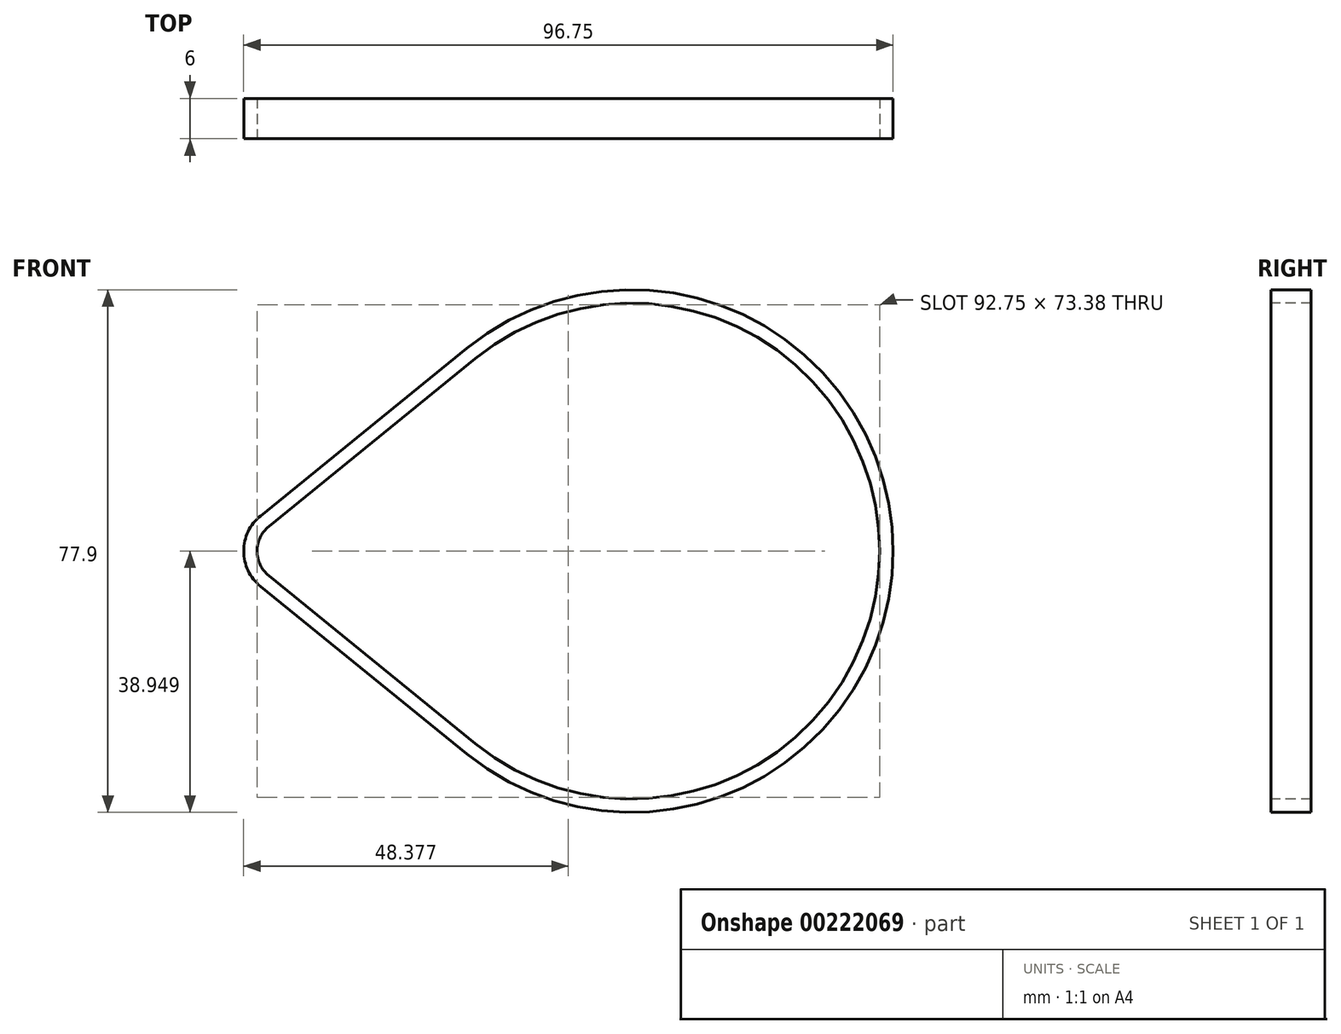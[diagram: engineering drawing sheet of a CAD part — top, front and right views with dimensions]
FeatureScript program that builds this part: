
annotation { "Feature Type Name" : "Feature", "Feature Type Description" : "" }
export const myFeature = defineFeature(function(context is Context, id is Id, definition is map)
    precondition{}
    {
        {
            var Q0;
            Q0=qCreatedBy(makeId("Front.planeOp"),FACE);
            var sketch = newSketch(context, id + "F0", { "sketchPlane" : qUnion([Q0])});
            skArc(sketch, "E0", {"start": v(89.5, 33.54) * mm, "mid": v(151.38, 62.99) * mm, "end": v(89.5, 92.44) * mm});
            skArc(sketch, "E1", {"start": v(58.76, 67.45) * mm, "mid": v(56.63, 62.99) * mm, "end": v(58.76, 58.53) * mm});
            skLineSegment(sketch, "E2", {"start": v(58.76, 67.45) * mm, "end": v(89.5, 92.44) * mm});
            skLineSegment(sketch, "E3", {"start": v(58.76, 58.53) * mm, "end": v(89.5, 33.54) * mm});
            skSolve(sketch);
        }
        {
            var Q0;
            Q0=makeQuery(id+"F0.imprint","IMPRINT",FACE,{"disambiguationData":[TD([[makeQuery(id+"F0.imprint","IMPRINT",EDGE,{"derivedFrom":sQuery(id+"F0.wireOp",EDGE,"E0")}),1.0]])]});
            extrude(context, id + "F1", {"entities" : qUnion([Q0]), "depth" : 6 * mm});
        }
        {
            var Q0;
            Q0=makeQuery(id+"F1.opExtrude","CAP_FACE",FACE,{"disambiguationData":[OSD([sQuery(id+"F0.wireOp",EDGE,"E0"),sQuery(id+"F0.wireOp",EDGE,"E1"),sQuery(id+"F0.wireOp",EDGE,"E2"),sQuery(id+"F0.wireOp",EDGE,"E3")])],"isStart":false});
            var sketch = newSketch(context, id + "F2", { "sketchPlane" : qUnion([Q0])});
            skLineSegment(sketch, "E4.0", {"start": v(58.76, 67.45) * mm, "end": v(89.5, 92.44) * mm});
            skArc(sketch, "E4.1", {"start": v(89.5, 33.54) * mm, "mid": v(151.38, 62.99) * mm, "end": v(89.5, 92.44) * mm});
            skLineSegment(sketch, "E5.0", {"start": v(58.76, 58.53) * mm, "end": v(89.5, 33.54) * mm});
            skArc(sketch, "E6.0", {"start": v(58.76, 67.45) * mm, "mid": v(56.63, 62.99) * mm, "end": v(58.76, 58.53) * mm});
            skLineSegment(sketch, "E7.0", {"start": v(59.39, 66.67) * mm, "end": v(90.13, 91.66) * mm});
            skArc(sketch, "E7.1", {"start": v(59.39, 66.67) * mm, "mid": v(57.63, 62.99) * mm, "end": v(59.39, 59.3) * mm});
            skLineSegment(sketch, "E7.2", {"start": v(59.39, 59.3) * mm, "end": v(90.13, 34.32) * mm});
            skArc(sketch, "E7.3", {"start": v(90.13, 34.32) * mm, "mid": v(150.38, 62.99) * mm, "end": v(90.13, 91.66) * mm});
            skSolve(sketch);
        }
        {
            var Q0;
            Q0=makeQuery(id+"F2.imprint","IMPRINT",FACE,{"disambiguationData":[TD([[makeQuery(id+"F2.imprint","IMPRINT",EDGE,{"derivedFrom":sQuery(id+"F2.wireOp",EDGE,"E7.0")}),-1.0]])]});
            extrude(context, id + "F3", {"entities" : qUnion([Q0]), "operationType" : NewBodyOperationType.REMOVE, "oppositeDirection" : true, "depth" : 25 * mm});
        }
        {
            var Q0;
            Q0=makeQuery(id+"F1.opExtrude","CAP_FACE",FACE,{"disambiguationData":[OSD([sQuery(id+"F0.wireOp",EDGE,"E0"),sQuery(id+"F0.wireOp",EDGE,"E1"),sQuery(id+"F0.wireOp",EDGE,"E2"),sQuery(id+"F0.wireOp",EDGE,"E3")])],"isStart":false});
            var sketch = newSketch(context, id + "F4", { "sketchPlane" : qUnion([Q0])});
            skLineSegment(sketch, "E8.0", {"start": v(58.12, 68.23) * mm, "end": v(88.86, 93.21) * mm});
            skArc(sketch, "E8.1", {"start": v(58.12, 68.23) * mm, "mid": v(55.63, 62.99) * mm, "end": v(58.12, 57.75) * mm});
            skLineSegment(sketch, "E8.2", {"start": v(58.12, 57.75) * mm, "end": v(88.86, 32.76) * mm});
            skArc(sketch, "E8.3", {"start": v(88.86, 32.76) * mm, "mid": v(152.38, 62.99) * mm, "end": v(88.86, 93.21) * mm});
            skSolve(sketch);
        }
        {
            var Q0;
            Q0=makeQuery(id+"F4.imprint","IMPRINT",FACE,{"disambiguationData":[TD([[makeQuery(id+"F4.imprint","IMPRINT",EDGE,{"derivedFrom":sQuery(id+"F4.wireOp",EDGE,"E8.0")}),-1.0]])]});
            extrude(context, id + "F5", {"entities" : qUnion([Q0]), "operationType" : NewBodyOperationType.ADD, "oppositeDirection" : true, "depth" : 6 * mm});
        }
    });
